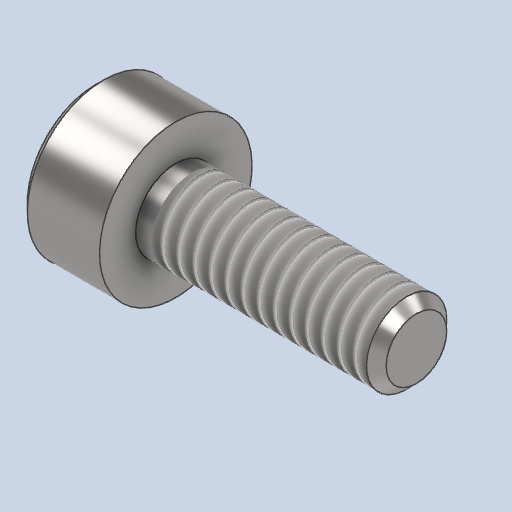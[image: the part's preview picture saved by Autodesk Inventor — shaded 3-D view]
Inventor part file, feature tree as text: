
AUTODESK INVENTOR PART (.ipt)
format: ipt  version: 2023 (Build 270158000, 158)  size: 210,432 bytes
history: native  units: mm
features: other x7, sketch x3, revolve x1, thread x1, hole x1, extrude x1
ambient origin geometry x8: Origin, YZ Plane, XZ Plane, XY Plane, X Axis, Y Axis, Z Axis, Center Point
bodies: Solid1 (feature_tree)
feature tree (14):
  revolve  "Revolution1"  [1 undecoded]
  thread  "Thread1"  [1 undecoded]
  hole  "Hole1"  [1 undecoded]
  extrude  "Extrusion1"  [1 undecoded]
  other  "to_cp_XY"
  other  "to_cp_YZ"
  other  "to_cp_ZX"
  other  "to_cp_X"
  other  "to_cp_Y"
  other  "to_cp_Z"
  other  "to_cp_Center"
  sketch  "Sketch_1"  dims[d0=360.0deg d1=5.3545mm d2=0.0mm]
  sketch  "Sketch2"  dims[d3=1.5mm d4=6.0mm d5=4.0mm d6=2.0mm d7=90.0deg d8=1.0mm d9=150.0deg d10=1.0mm d11=0.0mm]
  sketch  "Sketch_3"  dims[d12=0.0mm]
note: 4 required parameter values undecoded (feature->parameter linkage not recoverable at this tier; creation-order binding heuristic only, values carry confidence <= 0.55)